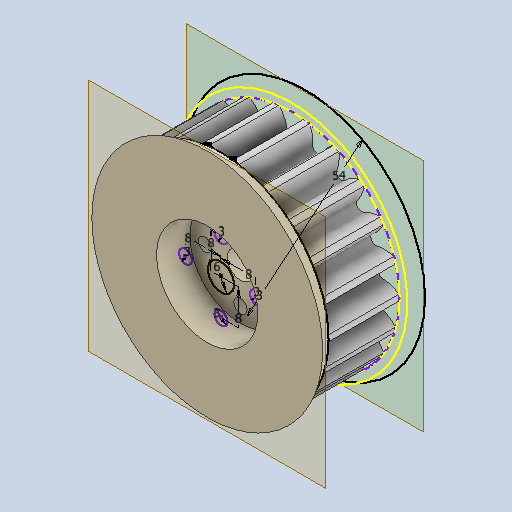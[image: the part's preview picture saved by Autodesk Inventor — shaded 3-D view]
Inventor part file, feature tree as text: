
AUTODESK INVENTOR PART (.ipt)
format: ipt  version: 2024.2 (Build 282272000, 272)  size: 478,208 bytes
history: native  units: mm
features: sketch x6, extrude x5, other x3, pattern_circular x1, loft x1, projected_geometry x1
ambient origin geometry x8: Origin, YZ Plane, XZ Plane, XY Plane, X Axis, Y Axis, Z Axis, Center Point
bodies: Body1 (feature_tree)
feature tree (17):
  other  "Твердое тело1"
  sketch  "Sketch1"  dims[d0=16.0mm d1=0.0mm d4=0.0mm d5=0.0mm d6=220.0mm d7=360.0deg d9=6.0mm d10=3.0mm d11=3.0mm d12=3.0mm d13=3.0mm d14=8.0mm d15=8.0mm d16=8.0mm d17=8.0mm d18=3.0mm d19=10.0mm d20=0.0mm d21=0.0mm d22=3.0mm d23=52.0mm d24=0.0mm d25=90.0deg d26=0.0mm d27=90.0deg d28=22.8mm d29=7.5mm d30=0.0mm d31=3.0mm d32=0.0mm d33=3.0mm d38=54.0mm]
  extrude  "Выдавливание1"  TaperAngle=0.0deg  [1 undecoded]
  extrude  "Выдавливание2"  TaperAngle=0.0deg  [1 undecoded]
  pattern_circular  "Круговой массив1"  Count=22 Angle=360.0deg
  extrude  "Выдавливание3"  Depth=10.0mm
  other  "РабПлоскость1"
  loft  "Лофт1"
  extrude  "Выдавливание4"  Depth=10.0mm
  extrude  "Выдавливание5"  Depth=10.0mm
  sketch  "Эскиз5"
  other  "РабПлоскость2"
  sketch  "Эскиз6"
  sketch  "Эскиз2"
  sketch  "Эскиз3"
  sketch  "Эскиз4"
  projected_geometry  "Спроецированная петля1"
note: 2 required parameter values undecoded (feature->parameter linkage not recoverable at this tier; creation-order binding heuristic only, values carry confidence <= 0.55)
